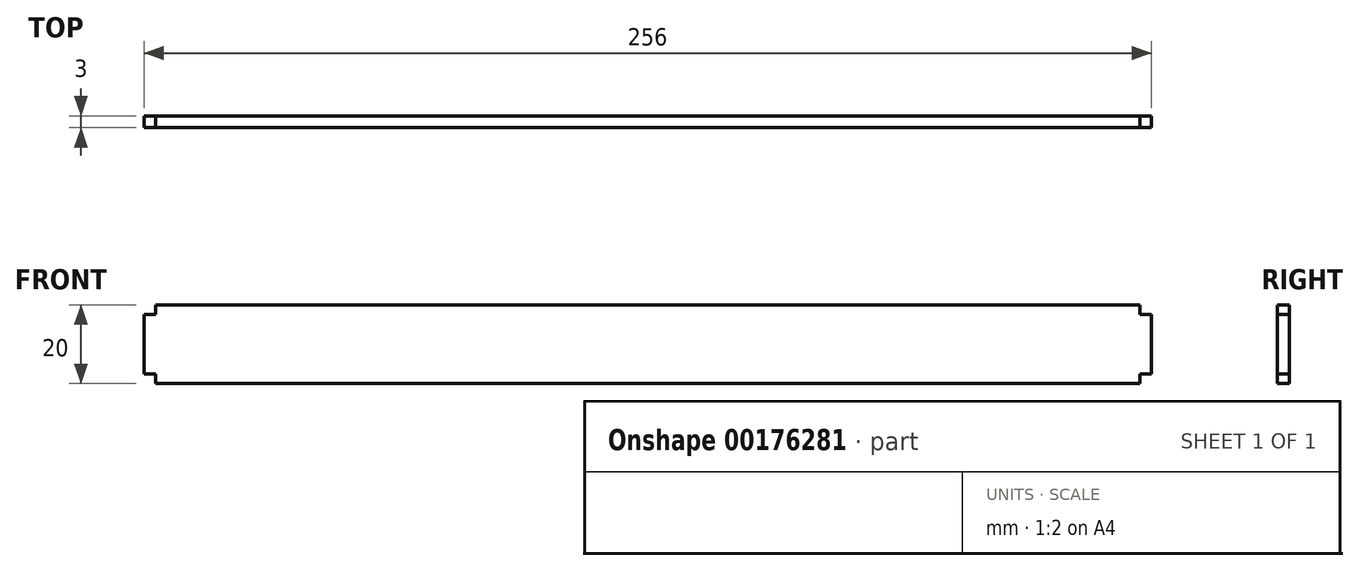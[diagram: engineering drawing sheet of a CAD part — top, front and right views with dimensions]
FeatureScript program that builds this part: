
annotation { "Feature Type Name" : "Feature", "Feature Type Description" : "" }
export const myFeature = defineFeature(function(context is Context, id is Id, definition is map)
    precondition{}
    {
        {
            var Q0;
            Q0=qCreatedBy(makeId("Front.planeOp"),FACE);
            var sketch = newSketch(context, id + "F0", { "sketchPlane" : qUnion([Q0])});
            skLineSegment(sketch, "E0.bottom", {"start": v(-125, 10) * mm, "end": v(125, 10) * mm});
            skLineSegment(sketch, "E0.top", {"start": v(-125, -10) * mm, "end": v(125, -10) * mm});
            skLineSegment(sketch, "E0.left", {"start": v(-125, 10) * mm, "end": v(-125, 7.5) * mm});
            skLineSegment(sketch, "E0.right", {"start": v(125, 10) * mm, "end": v(125, 7.5) * mm});
            skLineSegment(sketch, "E1.trimOffspring", {"start": v(-125, -7.5) * mm, "end": v(-125, -10) * mm});
            skLineSegment(sketch, "E2.trimOffspring", {"start": v(125, -7.5) * mm, "end": v(125, -10) * mm});
            skLineSegment(sketch, "E3", {"start": v(-125, 10) * mm, "end": v(125, -10) * mm, "construction": true});
            skLineSegment(sketch, "E4", {"start": v(125, 10) * mm, "end": v(-125, -10) * mm, "construction": true});
            skLineSegment(sketch, "E5.bottom", {"start": v(-128, 7.5) * mm, "end": v(-125, 7.5) * mm});
            skLineSegment(sketch, "E5.top", {"start": v(-128, -7.5) * mm, "end": v(-125, -7.5) * mm});
            skLineSegment(sketch, "E5.left", {"start": v(-128, 7.5) * mm, "end": v(-128, -7.5) * mm});
            skLineSegment(sketch, "E5.right", {"start": v(128, 7.5) * mm, "end": v(128, -7.5) * mm});
            skLineSegment(sketch, "E6.trimOffspring", {"start": v(125, 7.5) * mm, "end": v(128, 7.5) * mm});
            skLineSegment(sketch, "E7.trimOffspring", {"start": v(125, -7.5) * mm, "end": v(128, -7.5) * mm});
            skPoint(sketch, "E8", {"position": v(0, 0) * mm});
            skLineSegment(sketch, "E9", {"start": v(-128, 0) * mm, "end": v(0, 0) * mm, "construction": true});
            skSolve(sketch);
        }
        {
            var Q0;
            Q0 = qSketchRegion(id + "F0", true);
            extrude(context, id + "F1", {"entities" : qUnion([Q0]), "depth" : 3 * mm});
        }
    });
